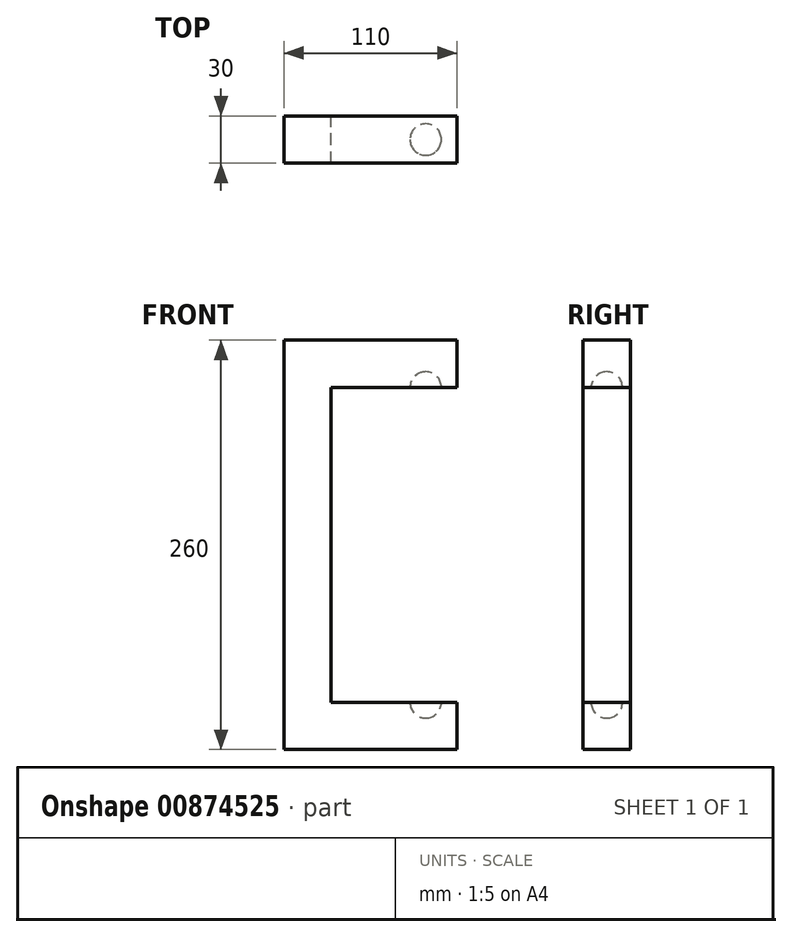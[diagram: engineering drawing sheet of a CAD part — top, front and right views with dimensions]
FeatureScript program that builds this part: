
annotation { "Feature Type Name" : "Feature", "Feature Type Description" : "" }
export const myFeature = defineFeature(function(context is Context, id is Id, definition is map)
    precondition{}
    {
        {
            var Q0;
            Q0=qCreatedBy(makeId("Front.planeOp"),FACE);
            var sketch = newSketch(context, id + "F0", { "sketchPlane" : qUnion([Q0])});
            skLineSegment(sketch, "E0", {"start": v(0, 30) * mm, "end": v(-80, 30) * mm});
            skLineSegment(sketch, "E1", {"start": v(-20, 30) * mm, "end": v(-20, 230) * mm, "construction": true});
            skLineSegment(sketch, "E2", {"start": v(-80, 30) * mm, "end": v(-80, 230) * mm});
            skLineSegment(sketch, "E3", {"start": v(-80, 230) * mm, "end": v(0, 230) * mm});
            skLineSegment(sketch, "E4", {"start": v(0, 230) * mm, "end": v(0, 260) * mm});
            skLineSegment(sketch, "E5", {"start": v(0, 260) * mm, "end": v(-110, 260) * mm});
            skLineSegment(sketch, "E6", {"start": v(-110, 260) * mm, "end": v(-110, 0) * mm});
            skLineSegment(sketch, "E7", {"start": v(-110, 0) * mm, "end": v(0, 0) * mm});
            skLineSegment(sketch, "E8", {"start": v(0, 0) * mm, "end": v(0, 30) * mm});
            skSolve(sketch);
        }
        {
            var Q0;
            Q0=qSketchRegion(id+"F0",true);
            extrude(context, id + "F1", {"entities" : qUnion([Q0]), "endBound" : BoundingType.SYMMETRIC, "depth" : 30 * mm, "offsetDistance" : 25 * mm});
        }
        {
            var Q0;
            Q0=qCreatedBy(makeId("Front.planeOp"),FACE);
            var sketch = newSketch(context, id + "F2", { "sketchPlane" : qUnion([Q0])});
            skLineSegment(sketch, "E9", {"start": v(-20, 20) * mm, "end": v(-20, 240) * mm, "construction": true});
            skArc(sketch, "E10", {"start": v(-20, 220) * mm, "mid": v(-10, 230) * mm, "end": v(-20, 240) * mm});
            skArc(sketch, "E11", {"start": v(-20, 20) * mm, "mid": v(-10, 30) * mm, "end": v(-20, 40) * mm});
            skLineSegment(sketch, "E12", {"start": v(-20, 240) * mm, "end": v(-20, 220) * mm});
            skLineSegment(sketch, "E13", {"start": v(-20, 40) * mm, "end": v(-20, 20) * mm});
            skSolve(sketch);
        }
        {
            var Q0;
            Q0=makeQuery(id+"F2.imprint","IMPRINT",FACE,{"disambiguationData":[TD([[makeQuery(id+"F2.imprint","IMPRINT",EDGE,{"derivedFrom":sQuery(id+"F2.wireOp",EDGE,"E11")}),1.0]])]});
            var Q1;
            Q1=makeQuery(id+"F2.imprint","IMPRINT",FACE,{"disambiguationData":[TD([[makeQuery(id+"F2.imprint","IMPRINT",EDGE,{"derivedFrom":sQuery(id+"F2.wireOp",EDGE,"E10")}),1.0]])]});
            var Q2;
            Q2=sQuery(id+"F2.wireOp",EDGE,"E10");
            var Q3;
            Q3=sQuery(id+"F2.wireOp",EDGE,"E11");
            var Q4;
            Q4=sQuery(id+"F2.wireOp",EDGE,"E9");
            revolve(context, id + "F3", {"operationType" : NewBodyOperationType.REMOVE, "surfaceOperationType" : NewSurfaceOperationType.NEW, "entities" : qUnion([Q0, Q1]), "surfaceEntities" : qUnion([Q2, Q3]), "axis" : qUnion([Q4]), "revolveType" : RevolveType.FULL});
        }
    });
